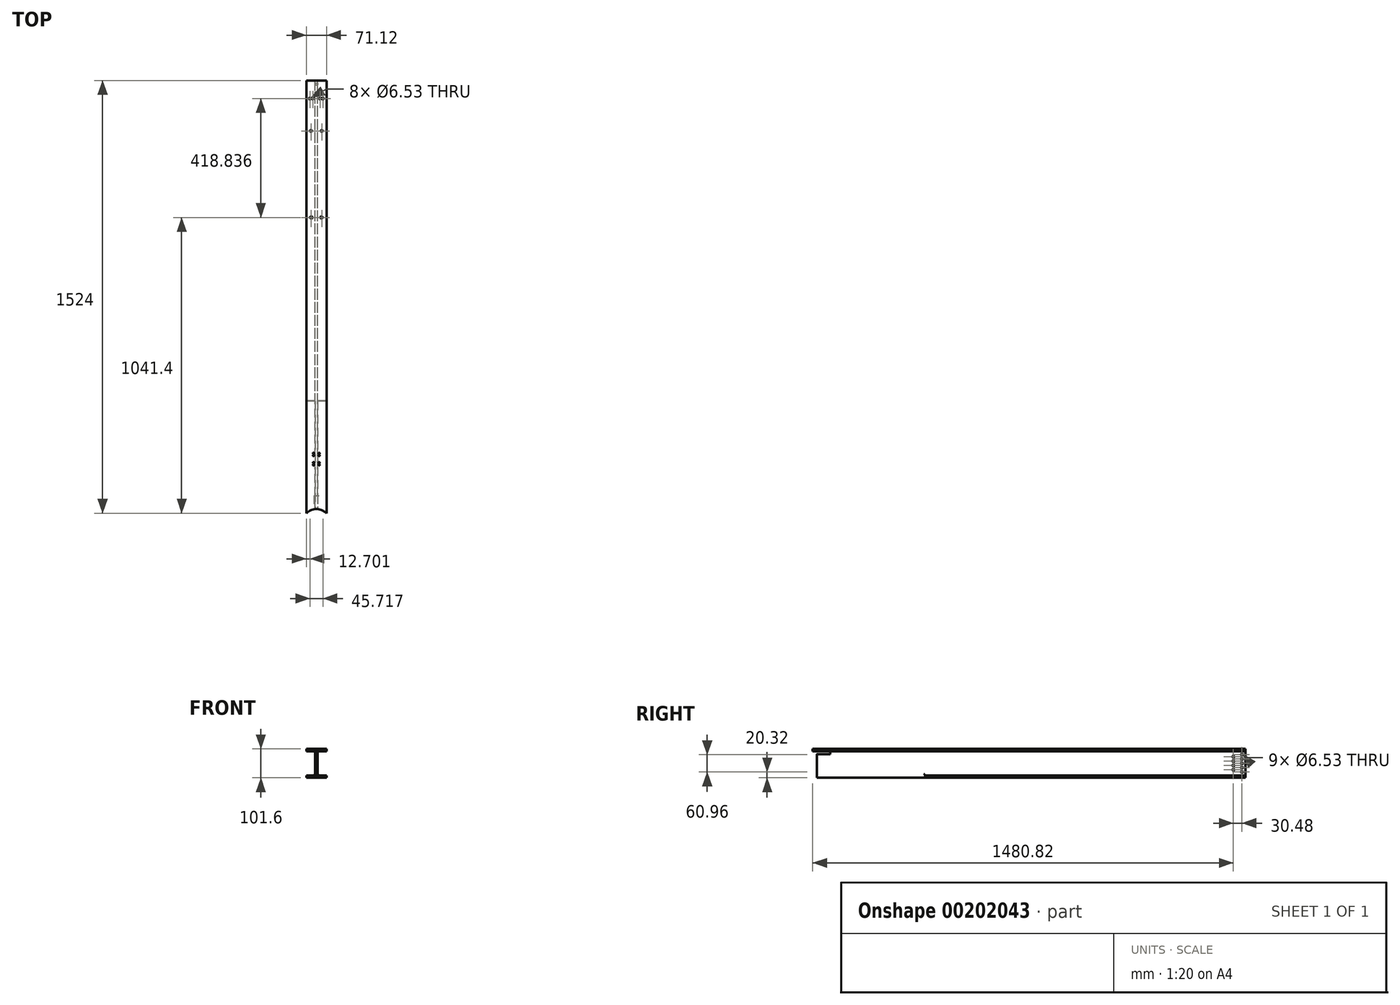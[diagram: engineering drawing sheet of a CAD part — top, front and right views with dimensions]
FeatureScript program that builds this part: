
annotation { "Feature Type Name" : "Feature", "Feature Type Description" : "" }
export const myFeature = defineFeature(function(context is Context, id is Id, definition is map)
    precondition{}
    {
        {
            var Q0;
            Q0=qCreatedBy(makeId("Front.planeOp"),FACE);
            var sketch = newSketch(context, id + "F0", { "sketchPlane" : qUnion([Q0])});
            skLineSegment(sketch, "E0.bottom", {"start": v(35.56, -50.8) * mm, "end": v(-35.56, -50.8) * mm});
            skLineSegment(sketch, "E0.top", {"start": v(35.56, 50.8) * mm, "end": v(-35.56, 50.8) * mm});
            skLineSegment(sketch, "E0.left", {"start": v(35.56, -50.8) * mm, "end": v(35.56, -42.42) * mm});
            skLineSegment(sketch, "E0.right", {"start": v(-35.56, -50.8) * mm, "end": v(-35.56, -42.42) * mm});
            skPoint(sketch, "E0.middle", {"position": v(0, 0) * mm});
            skLineSegment(sketch, "E1", {"start": v(-35.56, 50.8) * mm, "end": v(-35.56, 42.42) * mm});
            skLineSegment(sketch, "E2", {"start": v(-35.56, 42.42) * mm, "end": v(-4.2, 42.42) * mm});
            skLineSegment(sketch, "E3", {"start": v(0, 50.8) * mm, "end": v(-4.2, 50.8) * mm});
            skLineSegment(sketch, "E4", {"start": v(-4.2, 42.42) * mm, "end": v(-4.2, 0) * mm});
            skLineSegment(sketch, "E5.MirrorCS", {"start": v(4.2, 42.42) * mm, "end": v(4.2, 0) * mm});
            skLineSegment(sketch, "E6.MirrorCS", {"start": v(35.56, 50.8) * mm, "end": v(35.56, 42.42) * mm});
            skLineSegment(sketch, "E7.MirrorCS", {"start": v(-35.56, -42.42) * mm, "end": v(-4.2, -42.42) * mm});
            skLineSegment(sketch, "E8.MirrorCS", {"start": v(-4.2, -42.42) * mm, "end": v(-4.2, 0) * mm});
            skLineSegment(sketch, "E9.MirrorCS", {"start": v(4.2, -42.42) * mm, "end": v(4.2, 0) * mm});
            skPoint(sketch, "E10.orphan", {"position": v(0, -50.8) * mm});
            skLineSegment(sketch, "E11.trimOffspring", {"start": v(4.2, -42.42) * mm, "end": v(35.56, -42.42) * mm});
            skLineSegment(sketch, "E12.trimOffspring", {"start": v(4.2, 42.42) * mm, "end": v(35.56, 42.42) * mm});
            skLineSegment(sketch, "E13.trimOffspring", {"start": v(35.56, 42.42) * mm, "end": v(35.56, 50.8) * mm});
            skLineSegment(sketch, "E14.trimOffspring", {"start": v(-35.56, 42.42) * mm, "end": v(-35.56, 50.8) * mm});
            skSolve(sketch);
        }
        {
            var Q0;
            Q0=makeQuery(id+"F0.imprint","IMPRINT",FACE,{"disambiguationData":[TD([[makeQuery(id+"F0.imprint","IMPRINT",EDGE,{"derivedFrom":sQuery(id+"F0.wireOp",EDGE,"E0.bottom")}),-1.0]])]});
            extrude(context, id + "F1", {"entities" : qUnion([Q0]), "depth" : 1524 * mm});
        }
        {
            var Q0;
            Q0=makeQuery(id+"F1.opExtrude","SWEPT_EDGE",EDGE,{"disambiguationData":[OSD([sQuery(id+"F0.wireOp",EDGE,"E5.MirrorCS"),sQuery(id+"F0.wireOp",EDGE,"E12.trimOffspring")])]});
            var Q1;
            Q1=makeQuery(id+"F1.opExtrude","SWEPT_EDGE",EDGE,{"disambiguationData":[OSD([sQuery(id+"F0.wireOp",EDGE,"E9.MirrorCS"),sQuery(id+"F0.wireOp",EDGE,"E11.trimOffspring")])]});
            var Q2;
            Q2=makeQuery(id+"F1.opExtrude","SWEPT_EDGE",EDGE,{"disambiguationData":[OSD([sQuery(id+"F0.wireOp",EDGE,"E7.MirrorCS"),sQuery(id+"F0.wireOp",EDGE,"E8.MirrorCS")])]});
            var Q3;
            Q3=makeQuery(id+"F1.opExtrude","SWEPT_EDGE",EDGE,{"disambiguationData":[OSD([sQuery(id+"F0.wireOp",EDGE,"E2"),sQuery(id+"F0.wireOp",EDGE,"E4")])]});
            fillet(context, id + "F2", {"entities" : qUnion([Q0, Q1, Q2, Q3]), "radius" : 5.08 * mm, "tangentPropagation" : true, "allowEdgeOverflow" : false});
        }
        {
            var Q0;
            Q0=makeQuery(id+"F1.opExtrude","SWEPT_FACE",FACE,{"disambiguationData":[OSD([sQuery(id+"F0.wireOp",EDGE,"E0.top"),sQuery(id+"F0.wireOp",EDGE,"E3")])]});
            var sketch = newSketch(context, id + "F3", { "sketchPlane" : qUnion([Q0])});
            skLineSegment(sketch, "E15", {"start": v(0, -1524) * mm, "end": v(0, -1560.28) * mm});
            skPoint(sketch, "E15.endSnap0", {"position": v(0, -1524) * mm});
            skLineSegment(sketch, "E16", {"start": v(35.56, -1524) * mm, "end": v(0, -1560.28) * mm});
            skCircle(sketch, "E17", {"center": v(0, -1560.28) * mm, "radius": 50.8 * mm});
            skLineSegment(sketch, "E18.trimOffspring", {"start": v(0, -1611.08) * mm, "end": v(0, -1676.71) * mm});
            skSolve(sketch);
        }
        {
            var Q0;
            {var subQ6=sQuery(id+"F3.wireOp",EDGE,"E15");Q0=makeQuery(id+"F3.imprint","IMPRINT",FACE,{"disambiguationData":[TD([[makeQuery(id+"F3.imprint","IMPRINT",EDGE,{"derivedFrom":subQ6}),-1.0]])]});}
            var Q1;
            {var subQ0=sQuery(id+"F3.wireOp",EDGE,"E15");Q1=makeQuery(id+"F3.imprint","IMPRINT",FACE,{"disambiguationData":[TD([[makeQuery(id+"F3.imprint","IMPRINT",EDGE,{"derivedFrom":subQ0}),1.0]])]});}
            var Q2;
            {var subQ1=sQuery(id+"F0.wireOp",EDGE,"E0.top");var subQ2=makeQuery(id+"F1.opExtrude","CAP_EDGE",EDGE,{"disambiguationData":[OSD([subQ1,sQuery(id+"F0.wireOp",EDGE,"E3")])],"isStart":false});var subQ5=makeQuery(id+"F3.imprint","INTERSECT",VERTEX,{"derivedFrom":[subQ2,sQuery(id+"F3.wireOp",EDGE,"E15")]});Q2=makeQuery(id+"F3.imprint","IMPRINT",FACE,{"disambiguationData":[TD([[makeQuery(id+"F3.imprint","IMPRINT",EDGE,{"disambiguationData":[TD([[subQ5,-1.0]])],"derivedFrom":subQ2}),-1.0]])]});}
            extrude(context, id + "F4", {"entities" : qUnion([Q0, Q1, Q2]), "operationType" : NewBodyOperationType.REMOVE, "oppositeDirection" : true, "depth" : 101.6 * mm});
        }
        {
            var Q0;
            Q0=makeQuery(id+"F1.opExtrude","SWEPT_FACE",FACE,{"disambiguationData":[OSD([sQuery(id+"F0.wireOp",EDGE,"E5.MirrorCS"),sQuery(id+"F0.wireOp",EDGE,"E9.MirrorCS")])]});
            var sketch = newSketch(context, id + "F5", { "sketchPlane" : qUnion([Q0])});
            skSolve(sketch);
        }
        {
            var Q0;
            {var subQ0=sQuery(id+"F0.wireOp",EDGE,"E9.MirrorCS");var subQ1=sQuery(id+"F0.wireOp",EDGE,"E5.MirrorCS");Q0=makeQuery(id+"F5.imprint","IMPRINT",FACE,{"disambiguationData":[TD([[makeQuery(id+"F5.imprint","IMPRINT",EDGE,{"derivedFrom":makeQuery(id+"F1.opExtrude","CAP_EDGE",EDGE,{"disambiguationData":[OSD([subQ1,subQ0])],"isStart":true})}),1.0]])]});}
            var sketch = newSketch(context, id + "F6", { "sketchPlane" : qUnion([Q0])});
            skLineSegment(sketch, "E19", {"start": v(-1510.33, 42.42) * mm, "end": v(-1510.33, 32.26) * mm});
            skLineSegment(sketch, "E20", {"start": v(-1510.33, 32.26) * mm, "end": v(-1462.07, 32.26) * mm});
            skLineSegment(sketch, "E21", {"start": v(-1462.07, 32.26) * mm, "end": v(-1462.07, 42.42) * mm});
            skLineSegment(sketch, "E22", {"start": v(-1462.07, 42.42) * mm, "end": v(-1510.33, 42.42) * mm});
            skSolve(sketch);
        }
        {
            var Q0;
            Q0=qSketchRegion(id+"F6",true);
            extrude(context, id + "F7", {"entities" : qUnion([Q0]), "operationType" : NewBodyOperationType.REMOVE, "endBound" : BoundingType.SYMMETRIC, "oppositeDirection" : true, "depth" : 25.4 * mm});
        }
        {
            var Q0;
            Q0=makeQuery(id+"F7.boolean.opBoolean","INTERSECT",EDGE,{"derivedFrom":[makeQuery(id+"F4.boolean.opBoolean","COPY",FACE,{"derivedFrom":makeQuery(id+"F4.opExtrude","SWEPT_FACE",FACE,{"disambiguationData":[OSD([sQuery(id+"F3.wireOp",EDGE,"E17")])]})}),makeQuery(id+"F7.opExtrude","SWEPT_FACE",FACE,{"disambiguationData":[OSD([sQuery(id+"F6.wireOp",EDGE,"E20")])]})]});
            chamfer(context, id + "F8", {"entities" : qUnion([Q0]), "width" : 1.27 * mm, "tangentPropagation" : true});
        }
        {
            var Q0;
            Q0=makeQuery(id+"F1.opExtrude","SWEPT_FACE",FACE,{"disambiguationData":[OSD([sQuery(id+"F0.wireOp",EDGE,"E0.top"),sQuery(id+"F0.wireOp",EDGE,"E3")])]});
            var sketch = newSketch(context, id + "F9", { "sketchPlane" : qUnion([Q0])});
            skLineSegment(sketch, "E23", {"start": v(-0.26, -1524) * mm, "end": v(-0.26, -0.03) * mm});
            skLineSegment(sketch, "E24.bottom", {"start": v(9.71, -1353.82) * mm, "end": v(-10.23, -1353.82) * mm});
            skLineSegment(sketch, "E24.top", {"start": v(9.71, -1313.18) * mm, "end": v(-10.23, -1313.18) * mm});
            skLineSegment(sketch, "E25.bottom", {"start": v(9.71, -1346.2) * mm, "end": v(-10.23, -1346.2) * mm});
            skLineSegment(sketch, "E25.top", {"start": v(9.71, -1320.8) * mm, "end": v(-10.23, -1320.8) * mm});
            skLineSegment(sketch, "E26", {"start": v(35.56, -1524) * mm, "end": v(-35.56, -1524) * mm});
            skLineSegment(sketch, "E27", {"start": v(-0.26, -1524) * mm, "end": v(-0.26, -1353.82) * mm});
            skLineSegment(sketch, "E28", {"start": v(-0.26, -1353.82) * mm, "end": v(-0.26, -1346.2) * mm});
            skLineSegment(sketch, "E29", {"start": v(-0.26, -1346.2) * mm, "end": v(-0.26, -1320.8) * mm});
            skLineSegment(sketch, "E30", {"start": v(-0.26, -1320.8) * mm, "end": v(-0.26, -1313.18) * mm});
            skSolve(sketch);
        }
        {
            var Q0;
            Q0=sQuery(id+"F9.wireOp",VERTEX,"E24.bottom.end");
            var Q1;
            Q1=sQuery(id+"F9.wireOp",VERTEX,"E25.bottom.end");
            var Q2;
            Q2=sQuery(id+"F9.wireOp",VERTEX,"E25.top.end");
            var Q3;
            Q3=sQuery(id+"F9.wireOp",VERTEX,"E24.top.end");
            var Q4;
            Q4=sQuery(id+"F9.wireOp",VERTEX,"E24.top.start");
            var Q5;
            Q5=sQuery(id+"F9.wireOp",VERTEX,"E25.top.start");
            var Q6;
            Q6=sQuery(id+"F9.wireOp",VERTEX,"E25.bottom.start");
            var Q7;
            Q7=sQuery(id+"F9.wireOp",VERTEX,"E24.bottom.start");
            var Q8;
            Q8=makeQuery(id+"F1.opExtrude","SWEPT_BODY",BODY,{"disambiguationData":[OSD([sQuery(id+"F0.wireOp",EDGE,"E0.bottom"),sQuery(id+"F0.wireOp",EDGE,"E0.top"),sQuery(id+"F0.wireOp",EDGE,"E0.left"),sQuery(id+"F0.wireOp",EDGE,"E0.right"),sQuery(id+"F0.wireOp",EDGE,"E2"),sQuery(id+"F0.wireOp",EDGE,"E3"),sQuery(id+"F0.wireOp",EDGE,"E4"),sQuery(id+"F0.wireOp",EDGE,"E5.MirrorCS"),sQuery(id+"F0.wireOp",EDGE,"E7.MirrorCS"),sQuery(id+"F0.wireOp",EDGE,"E8.MirrorCS"),sQuery(id+"F0.wireOp",EDGE,"E9.MirrorCS"),sQuery(id+"F0.wireOp",EDGE,"E11.trimOffspring"),sQuery(id+"F0.wireOp",EDGE,"E12.trimOffspring"),sQuery(id+"F0.wireOp",EDGE,"E13.trimOffspring"),sQuery(id+"F0.wireOp",EDGE,"E14.trimOffspring")])]});
            hole(context, id + "F10", {"style" : HoleStyle.SIMPLE, "endStyle" : HoleEndStyle.BLIND, "standardTappedOrClearance" : lookupTablePath({ "standard" : "ANSI", "fit" : "Close", "size" : "#8", "type" : "Clearance" }), "standardBlindInLast" : lookupTablePath({ "fit" : "Close", "standard" : "ANSI", "size" : "#8", "type" : "Clearance" }), "holeDiameter" : 4.32 * mm, "holeDepth" : 25.4 * mm, "locations" : qUnion([Q0, Q1, Q2, Q3, Q4, Q5, Q6, Q7]), "scope" : qUnion([Q8])});
        }
        {
            var Q0;
            Q0=makeQuery(id+"F1.opExtrude","SWEPT_FACE",FACE,{"disambiguationData":[OSD([sQuery(id+"F0.wireOp",EDGE,"E0.bottom")])]});
            var sketch = newSketch(context, id + "F11", { "sketchPlane" : qUnion([Q0])});
            skLineSegment(sketch, "E31", {"start": v(4.2, 1509.65) * mm, "end": v(4.2, 1128.65) * mm});
            skLineSegment(sketch, "E32.bottom", {"start": v(4.2, 1128.65) * mm, "end": v(39.68, 1128.65) * mm});
            skLineSegment(sketch, "E32.top", {"start": v(4.2, 1528.41) * mm, "end": v(39.68, 1528.41) * mm});
            skLineSegment(sketch, "E32.left", {"start": v(4.2, 1128.65) * mm, "end": v(4.2, 1528.41) * mm});
            skLineSegment(sketch, "E32.right", {"start": v(39.68, 1128.65) * mm, "end": v(39.68, 1528.41) * mm});
            skLineSegment(sketch, "E33", {"start": v(0, 1526.52) * mm, "end": v(0, 1517.43) * mm});
            skLineSegment(sketch, "E34.MirrorCS", {"start": v(-4.2, 1528.41) * mm, "end": v(-39.68, 1528.41) * mm});
            skLineSegment(sketch, "E35.MirrorCS", {"start": v(-39.68, 1128.65) * mm, "end": v(-39.68, 1528.41) * mm});
            skLineSegment(sketch, "E36.MirrorCS", {"start": v(-4.2, 1128.65) * mm, "end": v(-4.2, 1528.41) * mm});
            skLineSegment(sketch, "E37.MirrorCS", {"start": v(-4.2, 1128.65) * mm, "end": v(-39.68, 1128.65) * mm});
            skSolve(sketch);
        }
        {
            var Q0;
            Q0=qSketchRegion(id+"F11",true);
            extrude(context, id + "F12", {"entities" : qUnion([Q0]), "operationType" : NewBodyOperationType.REMOVE, "oppositeDirection" : true, "depth" : 25.4 * mm});
        }
        {
            var Q0;
            Q0=makeQuery(id+"F12.boolean.opBoolean","COPY",EDGE,{"derivedFrom":makeQuery(id+"F12.opExtrude","SWEPT_EDGE",EDGE,{"disambiguationData":[OSD([sQuery(id+"F11.wireOp",EDGE,"E32.bottom"),sQuery(id+"F11.wireOp",EDGE,"E32.left")])]})});
            var Q1;
            Q1=makeQuery(id+"F12.boolean.opBoolean","COPY",EDGE,{"derivedFrom":makeQuery(id+"F12.opExtrude","SWEPT_EDGE",EDGE,{"disambiguationData":[OSD([sQuery(id+"F11.wireOp",EDGE,"E36.MirrorCS"),sQuery(id+"F11.wireOp",EDGE,"E37.MirrorCS")])]})});
            fillet(context, id + "F13", {"entities" : qUnion([Q0, Q1]), "radius" : 3.17 * mm, "tangentPropagation" : true, "allowEdgeOverflow" : false});
        }
        {
            var Q0;
            {var subQ0=sQuery(id+"F0.wireOp",EDGE,"E9.MirrorCS");var subQ1=sQuery(id+"F0.wireOp",EDGE,"E5.MirrorCS");Q0=makeQuery(id+"F5.imprint","IMPRINT",FACE,{"disambiguationData":[TD([[makeQuery(id+"F5.imprint","IMPRINT",EDGE,{"derivedFrom":makeQuery(id+"F1.opExtrude","CAP_EDGE",EDGE,{"disambiguationData":[OSD([subQ1,subQ0])],"isStart":true})}),1.0]])]});}
            var sketch = newSketch(context, id + "F14", { "sketchPlane" : qUnion([Q0])});
            skLineSegment(sketch, "E38", {"start": v(0, 37.34) * mm, "end": v(0, -37.34) * mm});
            skLineSegment(sketch, "E39", {"start": v(0, 0) * mm, "end": v(-30.48, 0) * mm});
            skLineSegment(sketch, "E40.bottom", {"start": v(-12.7, 30.48) * mm, "end": v(-48.26, 30.48) * mm});
            skLineSegment(sketch, "E40.top", {"start": v(-12.7, -30.48) * mm, "end": v(-48.26, -30.48) * mm});
            skLineSegment(sketch, "E40.left", {"start": v(-12.7, 30.48) * mm, "end": v(-12.7, -30.48) * mm});
            skLineSegment(sketch, "E40.right", {"start": v(-48.26, 30.48) * mm, "end": v(-48.26, -30.48) * mm});
            skPoint(sketch, "E40.middle", {"position": v(-30.48, 0) * mm});
            skLineSegment(sketch, "E41", {"start": v(-12.7, -30.48) * mm, "end": v(-12.7, -15.24) * mm});
            skLineSegment(sketch, "E42", {"start": v(-12.7, -15.24) * mm, "end": v(-12.7, 0) * mm});
            skLineSegment(sketch, "E43", {"start": v(-12.7, 0) * mm, "end": v(-12.7, 15.24) * mm});
            skLineSegment(sketch, "E44", {"start": v(-12.7, 15.24) * mm, "end": v(-12.7, 30.48) * mm});
            skLineSegment(sketch, "E45", {"start": v(-12.7, 30.48) * mm, "end": v(-43.18, 30.48) * mm});
            skLineSegment(sketch, "E46", {"start": v(-43.18, 30.48) * mm, "end": v(-43.18, 22.86) * mm});
            skLineSegment(sketch, "E47", {"start": v(-43.18, 22.86) * mm, "end": v(-43.18, 7.62) * mm});
            skLineSegment(sketch, "E48", {"start": v(-43.18, 7.62) * mm, "end": v(-43.18, -7.62) * mm});
            skLineSegment(sketch, "E49", {"start": v(-43.18, -7.62) * mm, "end": v(-43.18, -22.86) * mm});
            skSolve(sketch);
        }
        {
            var Q0;
            Q0=sQuery(id+"F14.wireOp",VERTEX,"E46.end");
            var Q1;
            Q1=sQuery(id+"F14.wireOp",VERTEX,"E47.end");
            var Q2;
            Q2=sQuery(id+"F14.wireOp",VERTEX,"E44.end");
            var Q3;
            Q3=sQuery(id+"F14.wireOp",VERTEX,"E43.end");
            var Q4;
            Q4=sQuery(id+"F14.wireOp",VERTEX,"E42.end");
            var Q5;
            Q5=sQuery(id+"F14.wireOp",VERTEX,"E41.end");
            var Q6;
            Q6=sQuery(id+"F14.wireOp",VERTEX,"E40.left.end");
            var Q7;
            Q7=sQuery(id+"F14.wireOp",VERTEX,"E49.start");
            var Q8;
            Q8=sQuery(id+"F14.wireOp",VERTEX,"E49.end");
            var Q9;
            Q9=makeQuery(id+"F1.opExtrude","SWEPT_BODY",BODY,{"disambiguationData":[OSD([sQuery(id+"F0.wireOp",EDGE,"E0.bottom"),sQuery(id+"F0.wireOp",EDGE,"E0.top"),sQuery(id+"F0.wireOp",EDGE,"E0.left"),sQuery(id+"F0.wireOp",EDGE,"E0.right"),sQuery(id+"F0.wireOp",EDGE,"E2"),sQuery(id+"F0.wireOp",EDGE,"E3"),sQuery(id+"F0.wireOp",EDGE,"E4"),sQuery(id+"F0.wireOp",EDGE,"E5.MirrorCS"),sQuery(id+"F0.wireOp",EDGE,"E7.MirrorCS"),sQuery(id+"F0.wireOp",EDGE,"E8.MirrorCS"),sQuery(id+"F0.wireOp",EDGE,"E9.MirrorCS"),sQuery(id+"F0.wireOp",EDGE,"E11.trimOffspring"),sQuery(id+"F0.wireOp",EDGE,"E12.trimOffspring"),sQuery(id+"F0.wireOp",EDGE,"E13.trimOffspring"),sQuery(id+"F0.wireOp",EDGE,"E14.trimOffspring")])]});
            hole(context, id + "F15", {"style" : HoleStyle.SIMPLE, "endStyle" : HoleEndStyle.BLIND, "standardTappedOrClearance" : lookupTablePath({ "standard" : "ANSI", "fit" : "Close", "size" : "1/4", "type" : "Clearance" }), "standardBlindInLast" : lookupTablePath({ "fit" : "Close", "standard" : "ANSI", "size" : "1/4", "type" : "Clearance" }), "holeDiameter" : 6.53 * mm, "holeDepth" : 25.4 * mm, "locations" : qUnion([Q0, Q1, Q2, Q3, Q4, Q5, Q6, Q7, Q8]), "scope" : qUnion([Q9])});
        }
        {
            var Q0;
            Q0=makeQuery(id+"F1.opExtrude","SWEPT_FACE",FACE,{"disambiguationData":[OSD([sQuery(id+"F0.wireOp",EDGE,"E0.top"),sQuery(id+"F0.wireOp",EDGE,"E3")])]});
            var sketch = newSketch(context, id + "F16", { "sketchPlane" : qUnion([Q0])});
            skLineSegment(sketch, "E50", {"start": v(0, 0) * mm, "end": v(0, -63.76) * mm});
            skPoint(sketch, "E50.endSnap0", {"position": v(0, 0) * mm});
            skLineSegment(sketch, "E51", {"start": v(0, -63.76) * mm, "end": v(12.7, -63.76) * mm});
            skLineSegment(sketch, "E52", {"start": v(12.7, -63.76) * mm, "end": v(22.86, -63.94) * mm});
            skLineSegment(sketch, "E53.MirrorCS", {"start": v(0, -63.76) * mm, "end": v(-12.7, -63.76) * mm});
            skLineSegment(sketch, "E54.MirrorCS", {"start": v(-12.7, -63.76) * mm, "end": v(-22.86, -63.94) * mm});
            skSolve(sketch);
        }
        {
            var Q0;
            Q0=sQuery(id+"F16.wireOp",VERTEX,"E54.MirrorCS.end");
            var Q1;
            Q1=sQuery(id+"F16.wireOp",VERTEX,"E53.MirrorCS.end");
            var Q2;
            Q2=sQuery(id+"F16.wireOp",VERTEX,"E51.end");
            var Q3;
            Q3=sQuery(id+"F16.wireOp",VERTEX,"E52.end");
            var Q4;
            Q4=makeQuery(id+"F1.opExtrude","SWEPT_BODY",BODY,{"disambiguationData":[OSD([sQuery(id+"F0.wireOp",EDGE,"E0.bottom"),sQuery(id+"F0.wireOp",EDGE,"E0.top"),sQuery(id+"F0.wireOp",EDGE,"E0.left"),sQuery(id+"F0.wireOp",EDGE,"E0.right"),sQuery(id+"F0.wireOp",EDGE,"E2"),sQuery(id+"F0.wireOp",EDGE,"E3"),sQuery(id+"F0.wireOp",EDGE,"E4"),sQuery(id+"F0.wireOp",EDGE,"E5.MirrorCS"),sQuery(id+"F0.wireOp",EDGE,"E7.MirrorCS"),sQuery(id+"F0.wireOp",EDGE,"E8.MirrorCS"),sQuery(id+"F0.wireOp",EDGE,"E9.MirrorCS"),sQuery(id+"F0.wireOp",EDGE,"E11.trimOffspring"),sQuery(id+"F0.wireOp",EDGE,"E12.trimOffspring"),sQuery(id+"F0.wireOp",EDGE,"E13.trimOffspring"),sQuery(id+"F0.wireOp",EDGE,"E14.trimOffspring")])]});
            hole(context, id + "F17", {"style" : HoleStyle.SIMPLE, "endStyle" : HoleEndStyle.BLIND, "standardTappedOrClearance" : lookupTablePath({ "standard" : "ANSI", "fit" : "Close", "size" : "1/4", "type" : "Clearance" }), "standardBlindInLast" : lookupTablePath({ "fit" : "Close", "standard" : "ANSI", "size" : "1/4", "type" : "Clearance" }), "holeDiameter" : 6.53 * mm, "holeDepth" : 25.4 * mm, "locations" : qUnion([Q0, Q1, Q2, Q3]), "scope" : qUnion([Q4])});
        }
        {
            var Q0;
            Q0=makeQuery(id+"F1.opExtrude","SWEPT_FACE",FACE,{"disambiguationData":[OSD([sQuery(id+"F0.wireOp",EDGE,"E0.top"),sQuery(id+"F0.wireOp",EDGE,"E3")])]});
            var sketch = newSketch(context, id + "F18", { "sketchPlane" : qUnion([Q0])});
            skLineSegment(sketch, "E55", {"start": v(0, 0) * mm, "end": v(0, -177.8) * mm});
            skPoint(sketch, "E55.endSnap0", {"position": v(0, 0) * mm});
            skLineSegment(sketch, "E56", {"start": v(0, -177.8) * mm, "end": v(-19.05, -177.8) * mm});
            skLineSegment(sketch, "E57", {"start": v(-19.05, -177.8) * mm, "end": v(19.05, -177.8) * mm});
            skLineSegment(sketch, "E58", {"start": v(19.05, -177.8) * mm, "end": v(0, -177.8) * mm});
            skLineSegment(sketch, "E59", {"start": v(0, -177.8) * mm, "end": v(0, -482.6) * mm});
            skLineSegment(sketch, "E60", {"start": v(0, -482.6) * mm, "end": v(-19.05, -482.6) * mm});
            skLineSegment(sketch, "E61", {"start": v(-19.05, -482.6) * mm, "end": v(19.05, -482.6) * mm});
            skSolve(sketch);
        }
        {
            var Q0;
            Q0=sQuery(id+"F18.wireOp",VERTEX,"E57.end");
            var Q1;
            Q1=sQuery(id+"F18.wireOp",VERTEX,"E56.end");
            var Q2;
            Q2=sQuery(id+"F18.wireOp",VERTEX,"E61.start");
            var Q3;
            Q3=sQuery(id+"F18.wireOp",VERTEX,"E61.end");
            var Q4;
            Q4=makeQuery(id+"F1.opExtrude","SWEPT_BODY",BODY,{"disambiguationData":[OSD([sQuery(id+"F0.wireOp",EDGE,"E0.bottom"),sQuery(id+"F0.wireOp",EDGE,"E0.top"),sQuery(id+"F0.wireOp",EDGE,"E0.left"),sQuery(id+"F0.wireOp",EDGE,"E0.right"),sQuery(id+"F0.wireOp",EDGE,"E2"),sQuery(id+"F0.wireOp",EDGE,"E3"),sQuery(id+"F0.wireOp",EDGE,"E4"),sQuery(id+"F0.wireOp",EDGE,"E5.MirrorCS"),sQuery(id+"F0.wireOp",EDGE,"E7.MirrorCS"),sQuery(id+"F0.wireOp",EDGE,"E8.MirrorCS"),sQuery(id+"F0.wireOp",EDGE,"E9.MirrorCS"),sQuery(id+"F0.wireOp",EDGE,"E11.trimOffspring"),sQuery(id+"F0.wireOp",EDGE,"E12.trimOffspring"),sQuery(id+"F0.wireOp",EDGE,"E13.trimOffspring"),sQuery(id+"F0.wireOp",EDGE,"E14.trimOffspring")])]});
            hole(context, id + "F19", {"style" : HoleStyle.SIMPLE, "endStyle" : HoleEndStyle.BLIND, "standardTappedOrClearance" : lookupTablePath({ "standard" : "ANSI", "fit" : "Close", "size" : "1/4", "type" : "Clearance" }), "standardBlindInLast" : lookupTablePath({ "fit" : "Close", "standard" : "ANSI", "size" : "1/4", "type" : "Clearance" }), "holeDiameter" : 6.53 * mm, "holeDepth" : 25.4 * mm, "locations" : qUnion([Q0, Q1, Q2, Q3]), "scope" : qUnion([Q4])});
        }
        {
            var Q0;
            Q0=makeQuery(id+"F1.opExtrude","SWEPT_FACE",FACE,{"disambiguationData":[OSD([sQuery(id+"F0.wireOp",EDGE,"E0.bottom")])]});
            var sketch = newSketch(context, id + "F20", { "sketchPlane" : qUnion([Q0])});
            skLineSegment(sketch, "E62", {"start": v(0, 0) * mm, "end": v(0, 482.6) * mm});
            skPoint(sketch, "E62.endSnap0", {"position": v(0, 0) * mm});
            skLineSegment(sketch, "E63", {"start": v(0, 482.6) * mm, "end": v(15.88, 482.6) * mm});
            skLineSegment(sketch, "E64", {"start": v(15.88, 482.6) * mm, "end": v(-15.88, 482.6) * mm});
            skSolve(sketch);
        }
        {
            var Q0;
            Q0=sQuery(id+"F20.wireOp",VERTEX,"E64.start");
            var Q1;
            Q1=sQuery(id+"F20.wireOp",VERTEX,"E64.end");
            var Q2;
            Q2=makeQuery(id+"F1.opExtrude","SWEPT_BODY",BODY,{"disambiguationData":[OSD([sQuery(id+"F0.wireOp",EDGE,"E0.bottom"),sQuery(id+"F0.wireOp",EDGE,"E0.top"),sQuery(id+"F0.wireOp",EDGE,"E0.left"),sQuery(id+"F0.wireOp",EDGE,"E0.right"),sQuery(id+"F0.wireOp",EDGE,"E2"),sQuery(id+"F0.wireOp",EDGE,"E3"),sQuery(id+"F0.wireOp",EDGE,"E4"),sQuery(id+"F0.wireOp",EDGE,"E5.MirrorCS"),sQuery(id+"F0.wireOp",EDGE,"E7.MirrorCS"),sQuery(id+"F0.wireOp",EDGE,"E8.MirrorCS"),sQuery(id+"F0.wireOp",EDGE,"E9.MirrorCS"),sQuery(id+"F0.wireOp",EDGE,"E11.trimOffspring"),sQuery(id+"F0.wireOp",EDGE,"E12.trimOffspring"),sQuery(id+"F0.wireOp",EDGE,"E13.trimOffspring"),sQuery(id+"F0.wireOp",EDGE,"E14.trimOffspring")])]});
            hole(context, id + "F21", {"style" : HoleStyle.SIMPLE, "endStyle" : HoleEndStyle.BLIND, "standardTappedOrClearance" : lookupTablePath({ "standard" : "ANSI", "fit" : "Close", "size" : "3/8", "type" : "Clearance" }), "standardBlindInLast" : lookupTablePath({ "fit" : "Close", "standard" : "ANSI", "size" : "3/8", "type" : "Clearance" }), "holeDiameter" : 9.8 * mm, "holeDepth" : 25.4 * mm, "locations" : qUnion([Q0, Q1]), "scope" : qUnion([Q2])});
        }
    });
